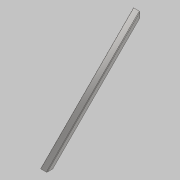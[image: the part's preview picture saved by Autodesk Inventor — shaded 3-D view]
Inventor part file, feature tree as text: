
AUTODESK INVENTOR PART (.ipt)
format: ipt  version: 2021 (Build 250183000, 183)  size: 110,592 bytes
history: native  units: mm
features: sweep x1, fillet x1, mirror x1, split x1, other x1, sketch x1
ambient origin geometry x8: Origin, YZ Plane, XZ Plane, XY Plane, X Axis, Y Axis, Z Axis, Center Point
bodies: Solid1 (feature_tree)
feature tree (6):
  sweep  "Sweep1"
  fillet  "Fillet1"  Radius=25.0mm
  mirror  "mirrored45"
  split  "Split1"
  other  "profile"
  sketch  "3D Sketch1"
